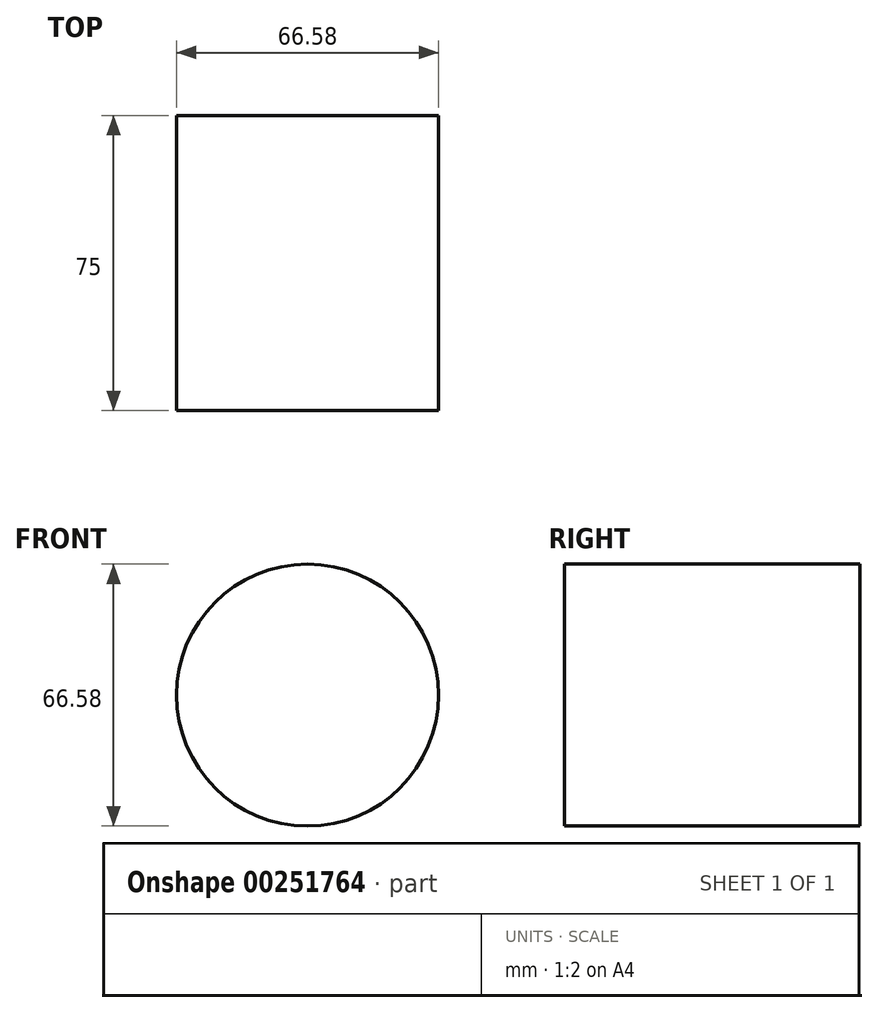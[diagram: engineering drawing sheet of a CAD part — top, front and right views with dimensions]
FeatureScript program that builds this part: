
annotation { "Feature Type Name" : "Feature", "Feature Type Description" : "" }
export const myFeature = defineFeature(function(context is Context, id is Id, definition is map)
    precondition{}
    {
        {
            var Q0;
            Q0=qCreatedBy(makeId("Front.planeOp"),FACE);
            var sketch = newSketch(context, id + "F0", { "sketchPlane" : qUnion([Q0])});
            skCircle(sketch, "E0", {"center": v(0, 0) * mm, "radius": 33.28 * mm});
            skSolve(sketch);
        }
        {
            var Q0;
            Q0 = qSketchRegion(id + "F0", true);
            extrude(context, id + "F1", {"entities" : qUnion([Q0]), "endBound" : BoundingType.SYMMETRIC, "depth" : 75 * mm});
        }
    });
